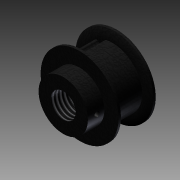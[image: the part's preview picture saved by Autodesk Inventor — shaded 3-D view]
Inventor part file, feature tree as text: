
AUTODESK INVENTOR PART (.ipt)
format: ipt  version: 2012 (Build 160160000, 160)  size: 196,608 bytes
history: native  units: in
note: dims shown in document units (in); Inventor stores cm internally (conversion verified against a paired STEP export)
features: extrude x1, thread x1, imported_body x1, sketch x1
ambient origin geometry x8: Origin, YZ Plane, XZ Plane, XY Plane, X Axis, Y Axis, Z Axis, Center Point
feature tree (4):
  extrude  "Extrusion1"  Depth=0.0787in
  thread  "Thread1"  [1 undecoded]
  imported_body  "Base1"
  sketch  "Sketch2"  dims[d1=0.0787in d2=0.0787in d3=0.0394in d4=0.3157in d5=0.2269in d6=0.3937in d7=0.0in d8=0.375in d9=0.3937in d10=0.0in]
note: 1 required parameter value undecoded (feature->parameter linkage not recoverable at this tier; creation-order binding heuristic only, values carry confidence <= 0.55)
